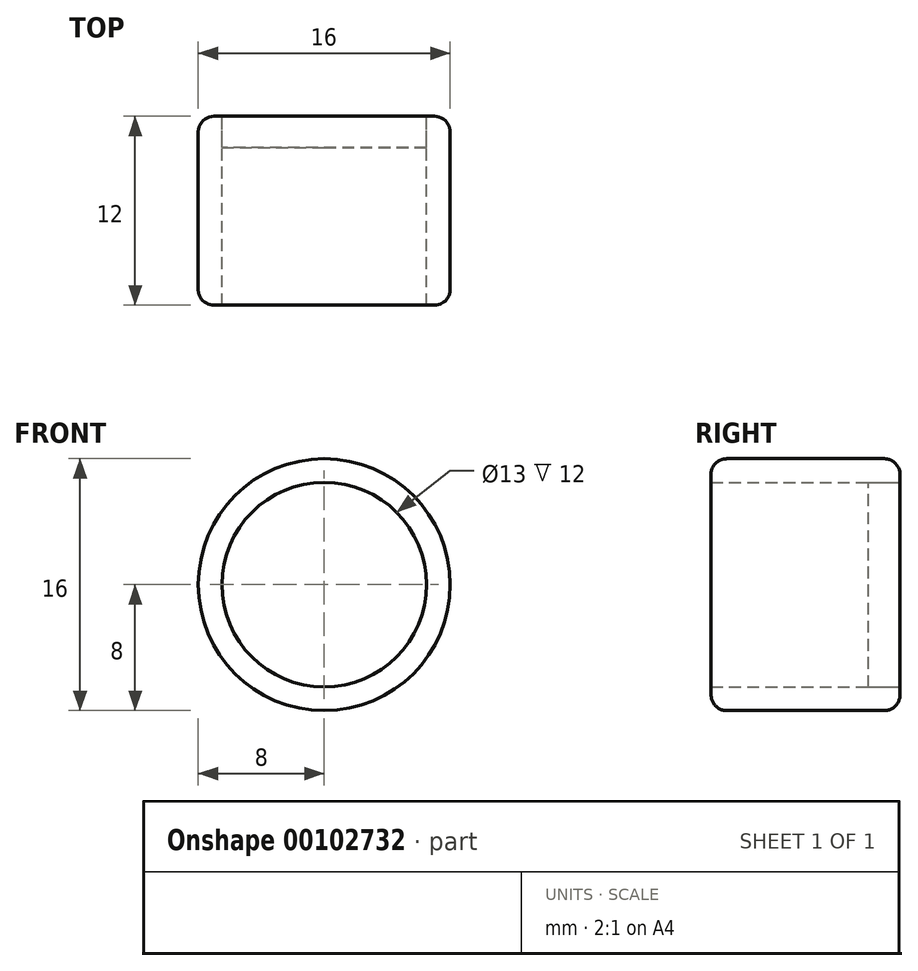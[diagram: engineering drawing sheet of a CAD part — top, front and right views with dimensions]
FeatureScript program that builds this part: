
annotation { "Feature Type Name" : "Feature", "Feature Type Description" : "" }
export const myFeature = defineFeature(function(context is Context, id is Id, definition is map)
    precondition{}
    {
        {
            var Q0;
            Q0=qCreatedBy(makeId("Front.planeOp"),FACE);
            var sketch = newSketch(context, id + "F0", { "sketchPlane" : qUnion([Q0])});
            skCircle(sketch, "E0", {"center": v(0, 0) * mm, "radius": 8 * mm});
            skCircle(sketch, "E1", {"center": v(0, 0) * mm, "radius": 6.5 * mm});
            skSolve(sketch);
        }
        {
            var Q0;
            Q0=makeQuery(id+"F0.imprint","IMPRINT",FACE,{"disambiguationData":[TD([[makeQuery(id+"F0.imprint","IMPRINT",EDGE,{"derivedFrom":sQuery(id+"F0.wireOp",EDGE,"E0")}),1.0]])]});
            extrude(context, id + "F1", {"entities" : qUnion([Q0]), "depth" : 12 * mm});
        }
        {
            var Q0;
            Q0=makeQuery(id+"F1.opExtrude","CAP_EDGE",EDGE,{"disambiguationData":[OSD([sQuery(id+"F0.wireOp",EDGE,"E0")])],"isStart":false});
            var Q1;
            Q1=makeQuery(id+"F1.opExtrude","CAP_EDGE",EDGE,{"disambiguationData":[OSD([sQuery(id+"F0.wireOp",EDGE,"E0")])],"isStart":true});
            fillet(context, id + "F2", {"entities" : qUnion([Q0, Q1]), "radius" : 1 * mm, "tangentPropagation" : true, "allowEdgeOverflow" : false});
        }
        {
            var Q0;
            Q0=makeQuery(id+"F1.opExtrude","CAP_FACE",FACE,{"disambiguationData":[OSD([sQuery(id+"F0.wireOp",EDGE,"E0"),sQuery(id+"F0.wireOp",EDGE,"E1")])],"isStart":true});
            var sketch = newSketch(context, id + "F3", { "sketchPlane" : qUnion([Q0])});
            skCircle(sketch, "E2", {"center": v(0, 0) * mm, "radius": 6.5 * mm});
            skSolve(sketch);
        }
        {
            var Q0;
            Q0=makeQuery(id+"F3.imprint","IMPRINT",FACE,{"disambiguationData":[TD([[makeQuery(id+"F3.imprint","IMPRINT",EDGE,{"derivedFrom":sQuery(id+"F3.wireOp",EDGE,"E2")}),-1.0]])]});
            extrude(context, id + "F4", {"entities" : qUnion([Q0]), "oppositeDirection" : true, "depth" : 2 * mm});
        }
    });
